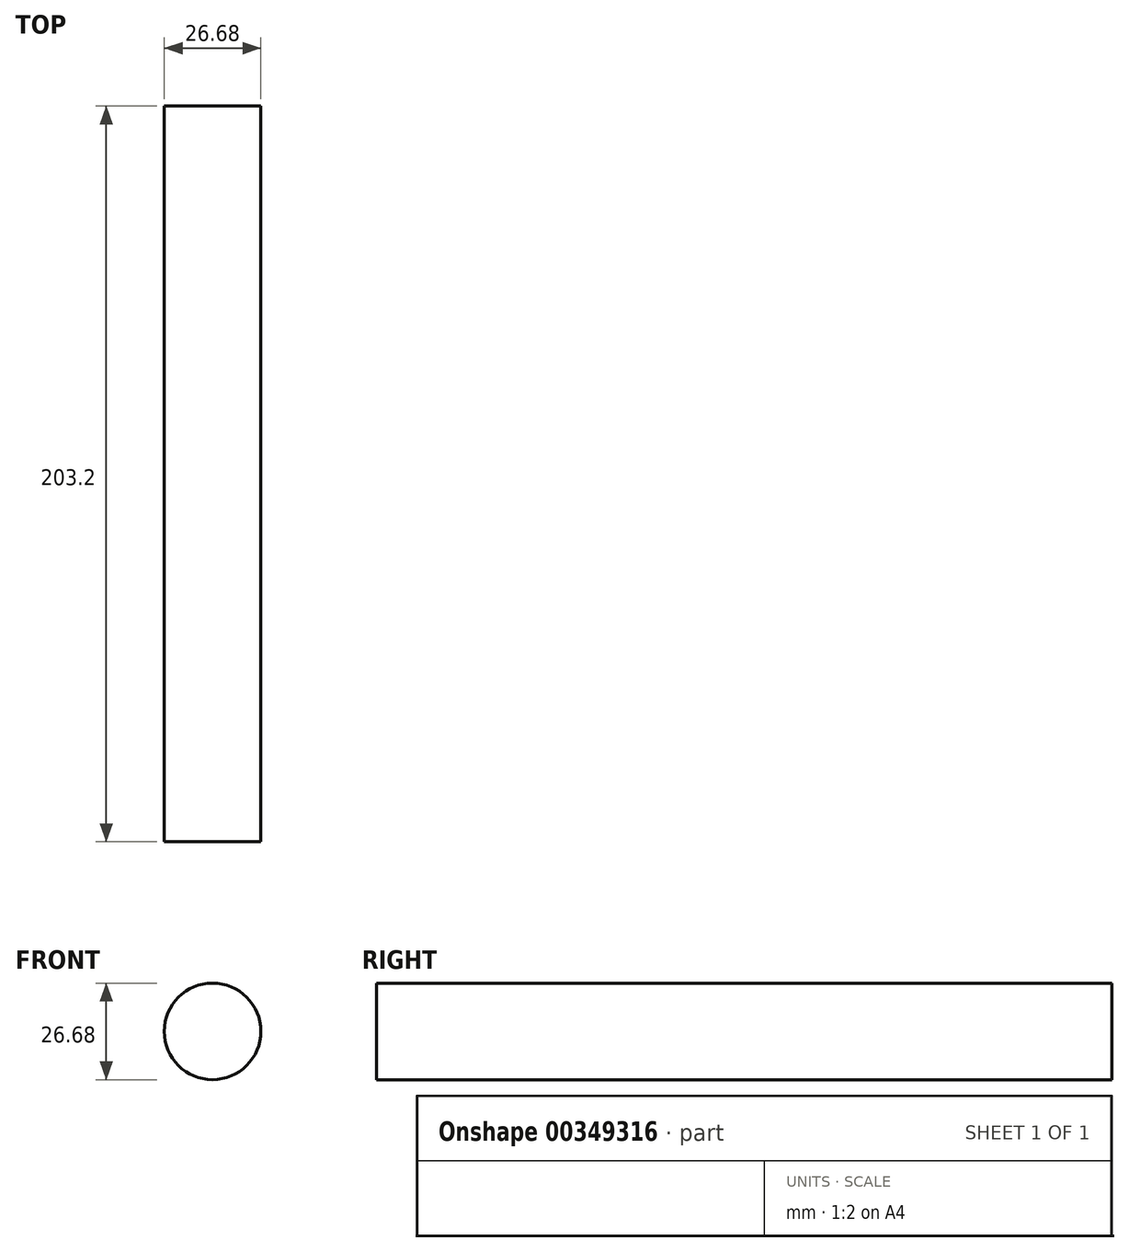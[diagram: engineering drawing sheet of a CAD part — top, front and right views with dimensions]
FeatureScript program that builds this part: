
annotation { "Feature Type Name" : "Feature", "Feature Type Description" : "" }
export const myFeature = defineFeature(function(context is Context, id is Id, definition is map)
    precondition{}
    {
        {
            var Q0;
            Q0=qCreatedBy(makeId("Front.planeOp"),FACE);
            var sketch = newSketch(context, id + "F0", { "sketchPlane" : qUnion([Q0])});
            skCircle(sketch, "E0", {"center": v(0, 0) * mm, "radius": 13.34 * mm});
            skSolve(sketch);
        }
        {
            var Q0;
            Q0 = qSketchRegion(id + "F0", true);
            extrude(context, id + "F1", {"entities" : qUnion([Q0]), "depth" : 203.2 * mm});
        }
    });
